# Revit family: QUEST HI-E DRY 195_Dehumidifiers
name_source: partatom
category: Mechanical Equipment
revit_build: Autodesk Revit 2016 (Build: 20150714_1515(x64)
units: mm (PartAtom-declared; Revit-internal decimal feet)

## family parameters
Always vertical = Yes
Cut with Voids When Loaded = No
OmniClass Number = 23.75.00.00
OmniClass Title = Climate Control (HVAC)
Part Type = Normal
Room Calculation Point = No
Round Connector Dimension = Use Diameter
Shared = No
Work Plane-Based = No

## types (1)
- QUEST HI-E DRY 195_Dehumidifiers
    Blower = 610 CFM @ 0.0" WG
    Current Draw = 13.1 amps.
    Efficiency = 5.4 PINTS/KWH
    Filters = 16”x20”x2” Pleated Media, (P/N 4021475)
 MERV-11
    Operating Temperature = 40°F Min - 110°F Max
    Pallet Quantity = 1 per pallet
    Part Number = 4036710
    Power = 1500 Watts @ 80°, 60%
    Power Cord = 10', 115 VOLT WITH GROUND
    Shipping Dimensions = 26”W x 47”H x 24”D
    Shipping Weight = 145 lbs.
    Supply Voltage = 115 VAC 5.9 amps
    Trap = Yes
    URL = www.questclimate.com/product/hi-e-dry-195/
    Unit Dimensions = 20”W x 36”H x 17”D
    Unit Weight = 130 lbs
    Warranty = Five years:1st year 100% of Parts and Labor
2nd-5th year 100% of Parts of sealed
refrigerant system
    Water Removal = 195 PINTS/DAY AT 80F, 60% RH
    Wireframe = Yes

## geometry (parser evidence)
native form markers: Sweep x7
no freeform markers — native parametric forms only
